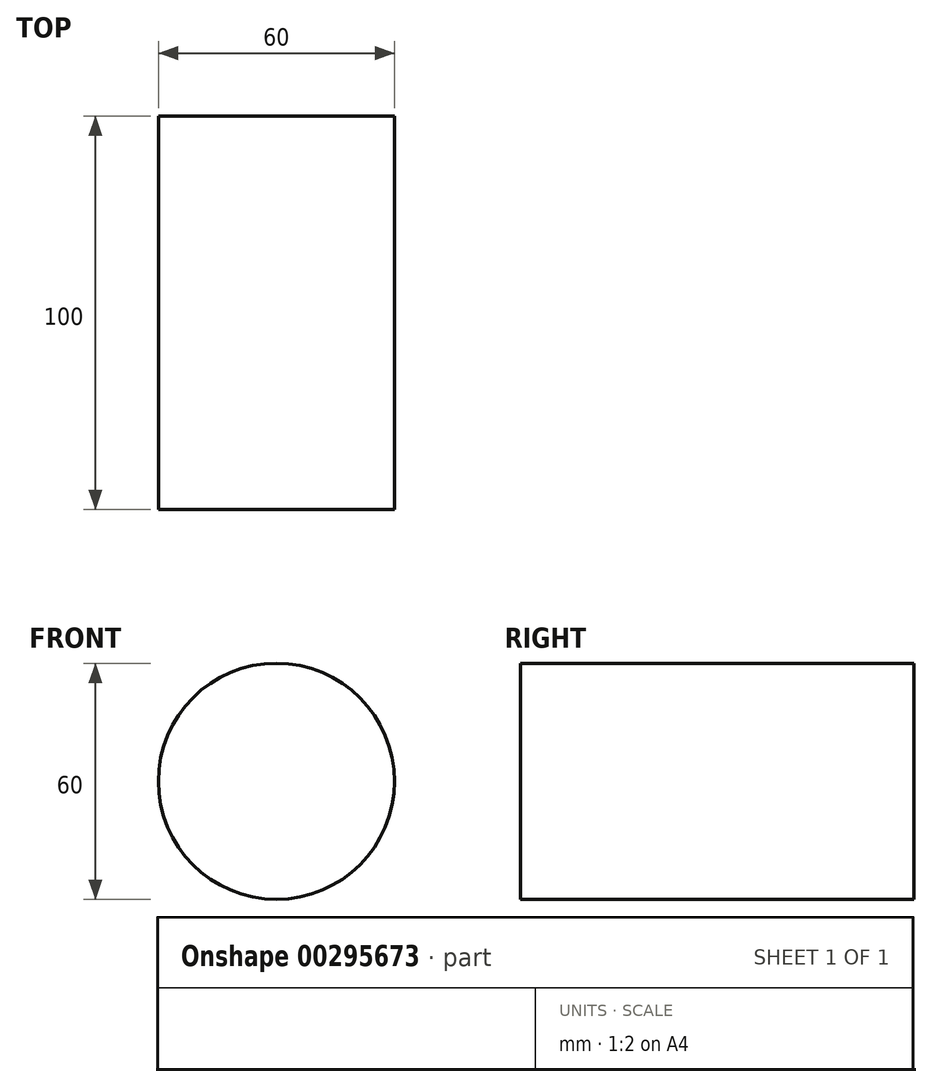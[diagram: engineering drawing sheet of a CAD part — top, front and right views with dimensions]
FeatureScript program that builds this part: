
annotation { "Feature Type Name" : "Feature", "Feature Type Description" : "" }
export const myFeature = defineFeature(function(context is Context, id is Id, definition is map)
    precondition{}
    {
        {
            var Q0;
            Q0=qCreatedBy(makeId("Front.planeOp"),FACE);
            var sketch = newSketch(context, id + "F0", { "sketchPlane" : qUnion([Q0])});
            skCircle(sketch, "E0", {"center": v(0, 0) * mm, "radius": 30 * mm});
            skSolve(sketch);
        }
        {
            var Q0;
            Q0 = qSketchRegion(id + "F0", true);
            extrude(context, id + "F1", {"entities" : qUnion([Q0]), "depth" : 100 * mm, "symmetric" : true});
        }
    });
